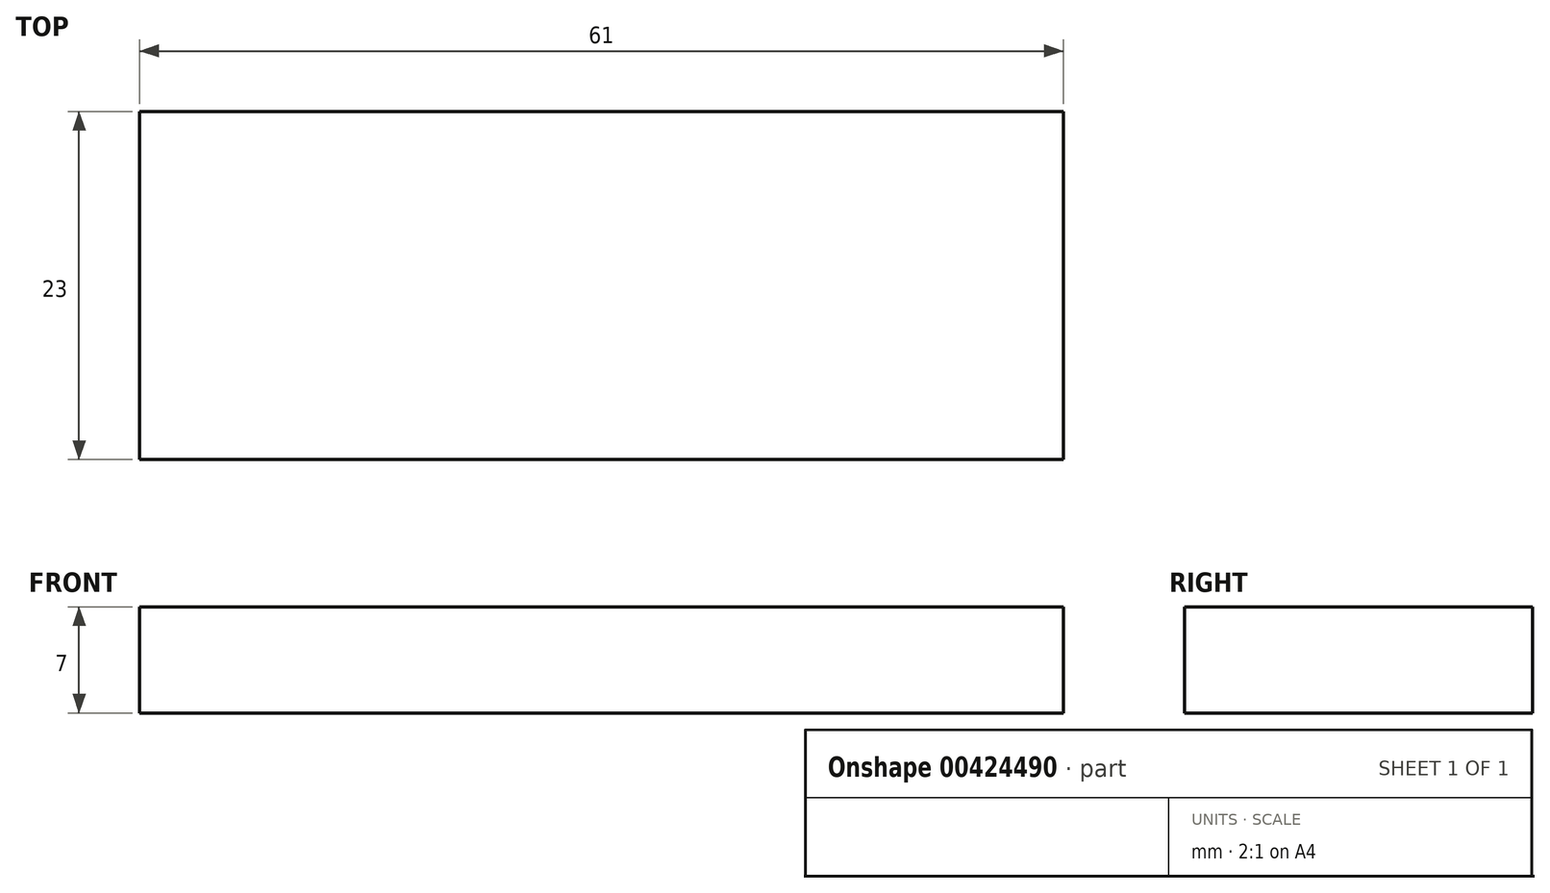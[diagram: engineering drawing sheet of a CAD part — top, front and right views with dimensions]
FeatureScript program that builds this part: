
annotation { "Feature Type Name" : "Feature", "Feature Type Description" : "" }
export const myFeature = defineFeature(function(context is Context, id is Id, definition is map)
    precondition{}
    {
        {
            var Q0;
            Q0=qCreatedBy(makeId("Top.planeOp"),FACE);
            var sketch = newSketch(context, id + "F0", { "sketchPlane" : qUnion([Q0])});
            skLineSegment(sketch, "E0.bottom", {"start": v(30.5, 11.5) * mm, "end": v(-30.5, 11.5) * mm});
            skLineSegment(sketch, "E0.top", {"start": v(30.5, -11.5) * mm, "end": v(-30.5, -11.5) * mm});
            skLineSegment(sketch, "E0.left", {"start": v(30.5, 11.5) * mm, "end": v(30.5, -11.5) * mm});
            skLineSegment(sketch, "E0.right", {"start": v(-30.5, 11.5) * mm, "end": v(-30.5, -11.5) * mm});
            skPoint(sketch, "E0.middle", {"position": v(0, 0) * mm});
            skSolve(sketch);
        }
        {
            var Q0;
            Q0 = qSketchRegion(id + "F0", true);
            extrude(context, id + "F1", {"entities" : qUnion([Q0]), "depth" : 7 * mm});
        }
    });
